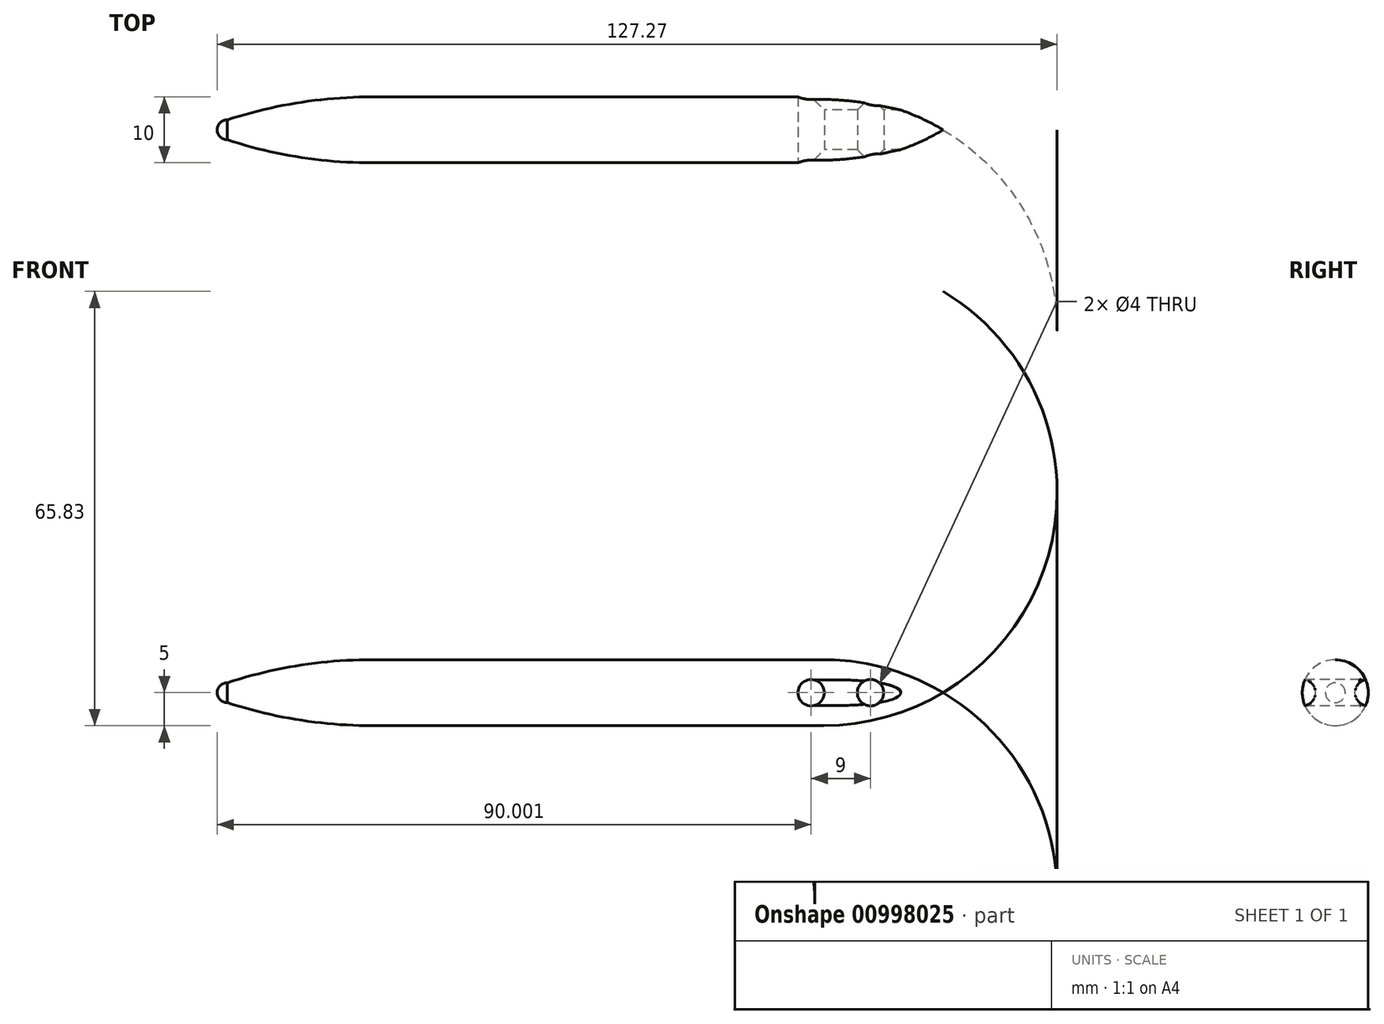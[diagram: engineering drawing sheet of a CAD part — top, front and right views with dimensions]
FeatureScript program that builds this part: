
annotation { "Feature Type Name" : "Feature", "Feature Type Description" : "" }
export const myFeature = defineFeature(function(context is Context, id is Id, definition is map)
    precondition{}
    {
        {
            var Q0;
            Q0=qCreatedBy(makeId("Top.planeOp"),FACE);
            var sketch = newSketch(context, id + "F0", { "sketchPlane" : qUnion([Q0])});
            skLineSegment(sketch, "E0.bottom", {"start": v(-36.12, 5) * mm, "end": v(32.24, 5) * mm});
            skLineSegment(sketch, "E0.top", {"start": v(-36.12, 0) * mm, "end": v(32.24, 0) * mm});
            skLineSegment(sketch, "E1.top", {"start": v(-58.12, 0) * mm, "end": v(-36.12, 0) * mm});
            skArc(sketch, "E2", {"start": v(-36.12, 5) * mm, "mid": v(-47.26, 4.12) * mm, "end": v(-58.12, 1.5) * mm});
            skLineSegment(sketch, "E3", {"start": v(-58.12, 0) * mm, "end": v(-59.62, 0) * mm});
            skArc(sketch, "E4", {"start": v(-58.12, 1.5) * mm, "mid": v(-59.18, 1.06) * mm, "end": v(-59.62, 0) * mm});
            skArc(sketch, "E5", {"start": v(50.38, 0) * mm, "mid": v(41.65, 3.73) * mm, "end": v(32.24, 5) * mm});
            skLineSegment(sketch, "E6", {"start": v(32.24, 0) * mm, "end": v(50.38, 0) * mm});
            skLineSegment(sketch, "E7", {"start": v(-72.26, 0) * mm, "end": v(58.11, 0) * mm, "construction": true});
            skSolve(sketch);
        }
        {
            var Q0;
            Q0=makeQuery(id+"F0.imprint","IMPRINT",FACE,{"disambiguationData":[TD([[makeQuery(id+"F0.imprint","IMPRINT",EDGE,{"derivedFrom":sQuery(id+"F0.wireOp",EDGE,"E0.bottom")}),-1.0]])]});
            var Q1;
            Q1=sQuery(id+"F0.wireOp",EDGE,"E7");
            revolve(context, id + "F1", {"surfaceOperationType" : NewSurfaceOperationType.NEW, "entities" : qUnion([Q0]), "axis" : qUnion([Q1]), "revolveType" : RevolveType.FULL});
        }
        {
            var Q0;
            Q0=qCreatedBy(makeId("Front.planeOp"),FACE);
            var sketch = newSketch(context, id + "F2", { "sketchPlane" : qUnion([Q0])});
            skCircle(sketch, "E8", {"center": v(30.38, 0) * mm, "radius": 2 * mm});
            skCircle(sketch, "E9", {"center": v(39.38, 0) * mm, "radius": 2 * mm});
            skSolve(sketch);
        }
        {
            var Q0;
            Q0 = qSketchRegion(id + "F2", true);
            extrude(context, id + "F3", {"entities" : qUnion([Q0]), "operationType" : NewBodyOperationType.REMOVE, "endBound" : BoundingType.SYMMETRIC, "oppositeDirection" : true, "depth" : 25 * mm, "offsetDistance" : 25 * mm});
        }
        {
            var Q0;
            Q0=qCreatedBy(makeId("Right.planeOp"),FACE);
            cPlane(context, id + "F4", {"entities" : qUnion([Q0]), "cplaneType" : CPlaneType.OFFSET, "offset" : 30 * mm, "width" : 150 * mm, "height" : 150 * mm});
        }
        {
            var Q0;
            Q0=qCreatedBy(id+"F4.planeOp",FACE);
            var sketch = newSketch(context, id + "F5", { "sketchPlane" : qUnion([Q0])});
            skCircle(sketch, "E10", {"center": v(5, 0) * mm, "radius": 2 * mm});
            skCircle(sketch, "E11", {"center": v(-5, 0) * mm, "radius": 2 * mm});
            skSolve(sketch);
        }
        {
            var Q0;
            Q0=makeQuery(id+"F5.imprint","IMPRINT",FACE,{"disambiguationData":[TD([[makeQuery(id+"F5.imprint","IMPRINT",EDGE,{"derivedFrom":sQuery(id+"F5.wireOp",EDGE,"E10")}),1.0]])]});
            var Q1;
            Q1=makeQuery(id+"F5.imprint","IMPRINT",FACE,{"disambiguationData":[TD([[makeQuery(id+"F5.imprint","IMPRINT",EDGE,{"derivedFrom":sQuery(id+"F5.wireOp",EDGE,"E11")}),1.0]])]});
            extrude(context, id + "F6", {"entities" : qUnion([Q0, Q1]), "operationType" : NewBodyOperationType.REMOVE, "depth" : 25 * mm, "offsetDistance" : 25 * mm});
        }
    });
